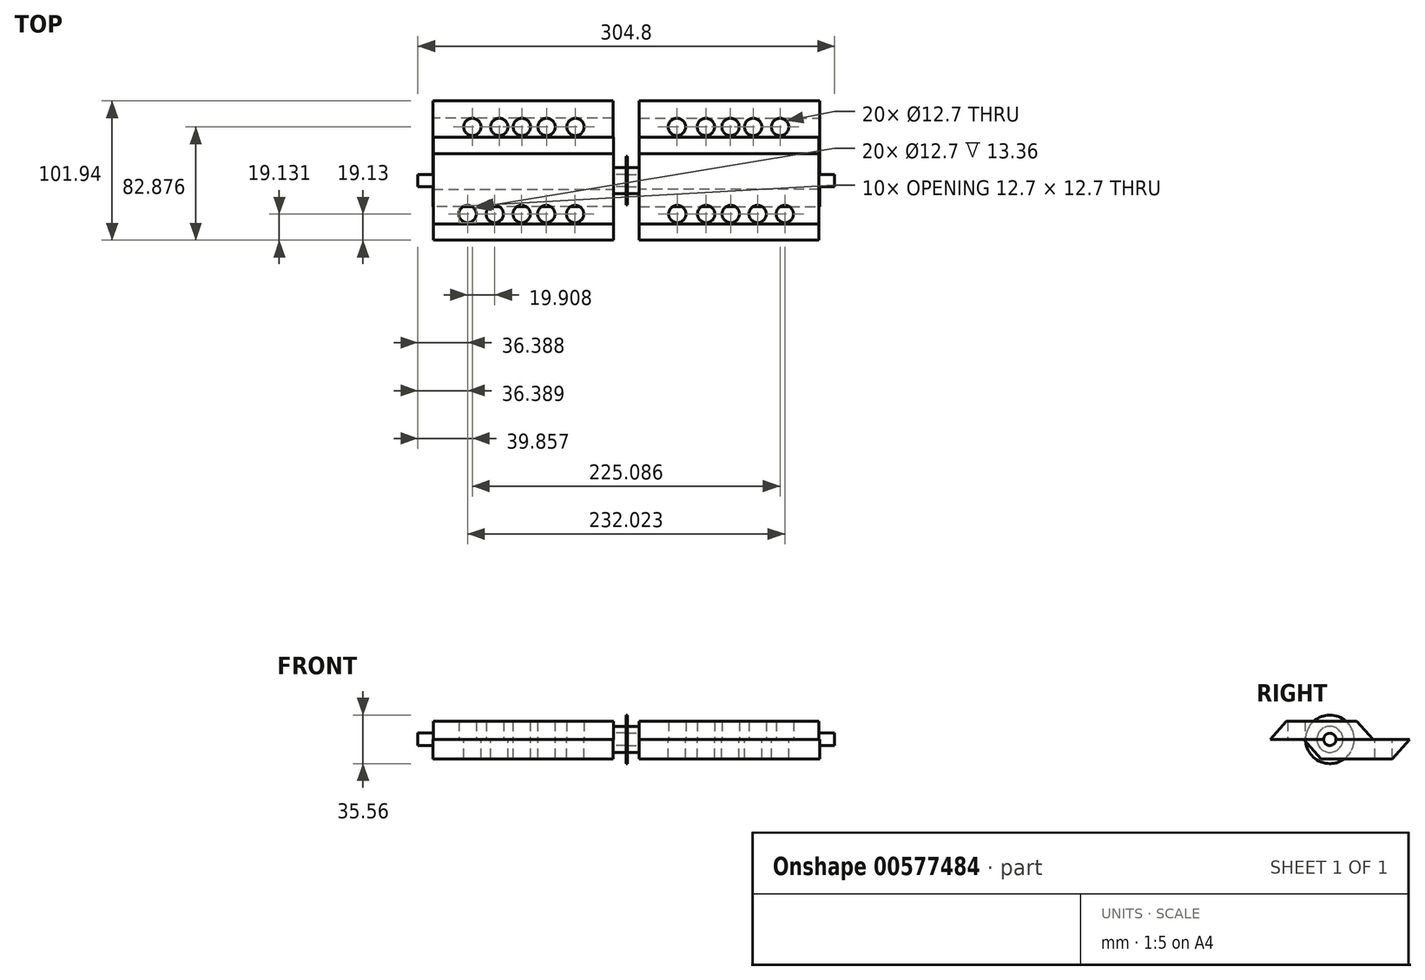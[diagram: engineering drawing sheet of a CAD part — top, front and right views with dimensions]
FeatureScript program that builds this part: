
annotation { "Feature Type Name" : "Feature", "Feature Type Description" : "" }
export const myFeature = defineFeature(function(context is Context, id is Id, definition is map)
    precondition{}
    {
        {
            var Q0;
            Q0=qCreatedBy(makeId("Right.planeOp"),FACE);
            var sketch = newSketch(context, id + "F0", { "sketchPlane" : qUnion([Q0])});
            skLineSegment(sketch, "E0", {"start": v(0, 0) * mm, "end": v(1.08, -4.4) * mm});
            skCircle(sketch, "E1", {"center": v(0, 0) * mm, "radius": 4.52 * mm});
            skSolve(sketch);
        }
        {
            var Q0;
            Q0=qSketchRegion(id+"F0",true);
            var Q1;
            Q1=qSketchRegion(id+"F3",true);
            var Q2;
            Q2=qSketchRegion(id+"F2",true);
            extrude(context, id + "F1", {"entities" : qUnion([Q0, Q1, Q2]), "depth" : 152.4 * mm, "offsetDistance" : 25.4 * mm});
        }
        {
            var Q0;
            Q0=qCreatedBy(makeId("Top.planeOp"),FACE);
            var sketch = newSketch(context, id + "F2", { "sketchPlane" : qUnion([Q0])});
            skLineSegment(sketch, "E2", {"start": v(0, 0) * mm, "end": v(9.53, 0) * mm});
            skLineSegment(sketch, "E3", {"start": v(9.53, 0) * mm, "end": v(9.53, -44.45) * mm});
            skLineSegment(sketch, "E4", {"start": v(9.53, -44.45) * mm, "end": v(141.3, -44.45) * mm});
            skSolve(sketch);
        }
        {
            var Q0;
            Q0=qCreatedBy(makeId("Top.planeOp"),FACE);
            var sketch = newSketch(context, id + "F3", { "sketchPlane" : qUnion([Q0])});
            skLineSegment(sketch, "E5", {"start": v(141.05, -43.51) * mm, "end": v(141.05, 32.69) * mm});
            skSolve(sketch);
        }
        {
            var Q0;
            Q0=qCreatedBy(makeId("Top.planeOp"),FACE);
            var sketch = newSketch(context, id + "F4", { "sketchPlane" : qUnion([Q0])});
            skLineSegment(sketch, "E6.bottom", {"start": v(9.32, -44.41) * mm, "end": v(140.97, -44.41) * mm});
            skLineSegment(sketch, "E6.top", {"start": v(9.32, 32.43) * mm, "end": v(140.97, 32.43) * mm});
            skLineSegment(sketch, "E6.left", {"start": v(9.32, -44.41) * mm, "end": v(9.32, 32.43) * mm});
            skLineSegment(sketch, "E6.right", {"start": v(140.97, -44.41) * mm, "end": v(140.97, 32.43) * mm});
            skSolve(sketch);
        }
        {
            var Q0;
            Q0=qSketchRegion(id+"F4",true);
            extrude(context, id + "F5", {"entities" : qUnion([Q0]), "operationType" : NewBodyOperationType.ADD, "depth" : 13.36 * mm, "offsetDistance" : 25.4 * mm});
        }
        {
            var Q0;
            Q0=makeQuery(id+"F5.opExtrude","CAP_EDGE",EDGE,{"disambiguationData":[OSD([sQuery(id+"F4.wireOp",EDGE,"E6.bottom")])],"isStart":false});
            chamfer(context, id + "F6", {"entities" : qUnion([Q0]), "chamferType" : ChamferType.TWO_OFFSETS, "width1" : 12.7 * mm, "oppositeDirection" : false, "width2" : 14.29 * mm, "tangentPropagation" : true});
        }
        {
            var Q0;
            Q0=makeQuery(id+"F5.opExtrude","CAP_EDGE",EDGE,{"disambiguationData":[OSD([sQuery(id+"F4.wireOp",EDGE,"E6.top")])],"isStart":false});
            chamfer(context, id + "F7", {"entities" : qUnion([Q0]), "chamferType" : ChamferType.TWO_OFFSETS, "width1" : 14.29 * mm, "oppositeDirection" : false, "width2" : 12.7 * mm, "tangentPropagation" : true});
        }
        {
            var Q0;
            Q0=qCreatedBy(makeId("Top.planeOp"),FACE);
            var sketch = newSketch(context, id + "F8", { "sketchPlane" : qUnion([Q0])});
            skLineSegment(sketch, "E7", {"start": v(9.57, 0) * mm, "end": v(9.57, -19.05) * mm});
            skLineSegment(sketch, "E8.bottom", {"start": v(9.57, -19.05) * mm, "end": v(141.48, -19.05) * mm});
            skLineSegment(sketch, "E8.top", {"start": v(9.57, 58.35) * mm, "end": v(141.48, 58.35) * mm});
            skLineSegment(sketch, "E8.left", {"start": v(9.57, -19.05) * mm, "end": v(9.57, 58.35) * mm});
            skLineSegment(sketch, "E8.right", {"start": v(141.48, -19.05) * mm, "end": v(141.48, 58.35) * mm});
            skSolve(sketch);
        }
        {
            var Q0;
            Q0=qSketchRegion(id+"F8",true);
            extrude(context, id + "F9", {"entities" : qUnion([Q0]), "operationType" : NewBodyOperationType.ADD, "oppositeDirection" : true, "depth" : 14.29 * mm, "offsetDistance" : 25.4 * mm});
        }
        {
            var Q0;
            Q0=makeQuery(id+"F9.opExtrude","CAP_EDGE",EDGE,{"disambiguationData":[OSD([sQuery(id+"F8.wireOp",EDGE,"E8.top")])],"isStart":false});
            chamfer(context, id + "F10", {"entities" : qUnion([Q0]), "chamferType" : ChamferType.TWO_OFFSETS, "width1" : 12.7 * mm, "oppositeDirection" : false, "width2" : 14.29 * mm, "tangentPropagation" : true});
        }
        {
            var Q0;
            Q0=makeQuery(id+"F9.opExtrude","CAP_EDGE",EDGE,{"disambiguationData":[OSD([sQuery(id+"F8.wireOp",EDGE,"E8.bottom")])],"isStart":false});
            chamfer(context, id + "F11", {"entities" : qUnion([Q0]), "chamferType" : ChamferType.TWO_OFFSETS, "width1" : 14.29 * mm, "oppositeDirection" : false, "width2" : 12.7 * mm, "tangentPropagation" : true});
        }
        {
            var Q0;
            Q0=qCreatedBy(makeId("Top.planeOp"),FACE);
            var sketch = newSketch(context, id + "F12", { "sketchPlane" : qUnion([Q0])});
            skPoint(sketch, "E9", {"position": v(76.3, 39.29) * mm});
            skPoint(sketch, "E10", {"position": v(92.85, 39.29) * mm});
            skPoint(sketch, "E11", {"position": v(112.54, 39.29) * mm});
            skPoint(sketch, "E12", {"position": v(58.24, 39.29) * mm});
            skPoint(sketch, "E13", {"position": v(37.1, 39.29) * mm});
            skSolve(sketch);
        }
        {
            var Q0;
            Q0=sQuery(id+"F12.wireOp",VERTEX,"E9");
            var Q1;
            Q1=sQuery(id+"F12.wireOp",VERTEX,"E10");
            var Q2;
            Q2=sQuery(id+"F12.wireOp",VERTEX,"E11");
            var Q3;
            Q3=sQuery(id+"F12.wireOp",VERTEX,"E12");
            var Q4;
            Q4=sQuery(id+"F12.wireOp",VERTEX,"E13");
            var Q5;
            Q5=makeQuery(id+"F1.opExtrude","SWEPT_BODY",BODY,{"disambiguationData":[OSD([sQuery(id+"F0.wireOp",EDGE,"E1")])]});
            hole(context, id + "F13", {"style" : HoleStyle.SIMPLE, "endStyle" : HoleEndStyle.THROUGH, "holeDiameter" : 12.7 * mm, "isTappedThrough" : true, "tappedDepth" : 12.7 * mm, "tapClearance" : 3, "locations" : qUnion([Q0, Q1, Q2, Q3, Q4]), "scope" : qUnion([Q5])});
        }
        {
            var Q0;
            Q0=qCreatedBy(makeId("Top.planeOp"),FACE);
            var sketch = newSketch(context, id + "F14", { "sketchPlane" : qUnion([Q0])});
            skPoint(sketch, "E14", {"position": v(76.48, -24.46) * mm});
            skPoint(sketch, "E15", {"position": v(96.1, -24.46) * mm});
            skPoint(sketch, "E16", {"position": v(116.01, -24.46) * mm});
            skPoint(sketch, "E17", {"position": v(58.48, -24.46) * mm});
            skPoint(sketch, "E18", {"position": v(37.37, -24.46) * mm});
            skSolve(sketch);
        }
        {
            var Q0;
            Q0=sQuery(id+"F14.wireOp",VERTEX,"E16");
            var Q1;
            Q1=sQuery(id+"F14.wireOp",VERTEX,"E15");
            var Q2;
            Q2=sQuery(id+"F14.wireOp",VERTEX,"E14");
            var Q3;
            Q3=sQuery(id+"F14.wireOp",VERTEX,"E18");
            var Q4;
            Q4=sQuery(id+"F14.wireOp",VERTEX,"E17");
            var Q5;
            Q5=makeQuery(id+"F1.opExtrude","SWEPT_BODY",BODY,{"disambiguationData":[OSD([sQuery(id+"F0.wireOp",EDGE,"E1")])]});
            hole(context, id + "F15", {"style" : HoleStyle.SIMPLE, "endStyle" : HoleEndStyle.THROUGH, "oppositeDirection" : true, "holeDiameter" : 12.7 * mm, "isTappedThrough" : true, "tappedDepth" : 12.7 * mm, "tapClearance" : 3, "locations" : qUnion([Q0, Q1, Q2, Q3, Q4]), "scope" : qUnion([Q5])});
        }
        {
            var Q0;
            Q0=makeQuery(id+"F1.opExtrude","SWEPT_BODY",BODY,{"disambiguationData":[OSD([sQuery(id+"F0.wireOp",EDGE,"E1")])]});
            var Q1;
            Q1=qCreatedBy(makeId("Right.planeOp"),FACE);
            mirror(context, id + "F16", {"operationType" : NewBodyOperationType.ADD, "entities" : qUnion([Q0]), "mirrorPlane" : qUnion([Q1])});
        }
        {
            var Q0;
            Q0=qCreatedBy(makeId("Right.planeOp"),FACE);
            var sketch = newSketch(context, id + "F17", { "sketchPlane" : qUnion([Q0])});
            skCircle(sketch, "E19", {"center": v(0, 0) * mm, "radius": 9.53 * mm});
            skSolve(sketch);
        }
        {
            var Q0;
            Q0=qSketchRegion(id+"F17",true);
            extrude(context, id + "F18", {"entities" : qUnion([Q0]), "operationType" : NewBodyOperationType.ADD, "depth" : 25.4 * mm, "offsetDistance" : 25.4 * mm});
        }
        {
            var Q0;
            Q0=makeQuery(id+"F1.opExtrude","SWEPT_BODY",BODY,{"disambiguationData":[OSD([sQuery(id+"F0.wireOp",EDGE,"E1")])]});
            var Q1;
            Q1=qCreatedBy(makeId("Right.planeOp"),FACE);
            mirror(context, id + "F19", {"entities" : qUnion([Q0]), "mirrorPlane" : qUnion([Q1])});
        }
        {
            var Q0;
            Q0=qCreatedBy(makeId("Right.planeOp"),FACE);
            var sketch = newSketch(context, id + "F20", { "sketchPlane" : qUnion([Q0])});
            skCircle(sketch, "E20", {"center": v(0, 0) * mm, "radius": 17.78 * mm});
            skSolve(sketch);
        }
        {
            var Q0;
            Q0=makeQuery(id+"F20.imprint","IMPRINT",FACE,{"disambiguationData":[TD([[makeQuery(id+"F20.imprint","IMPRINT",EDGE,{"derivedFrom":sQuery(id+"F20.wireOp",EDGE,"E20")}),1.0]])]});
            extrude(context, id + "F21", {"entities" : qUnion([Q0]), "depth" : 1.02 * mm, "offsetDistance" : 25.4 * mm});
        }
    });
